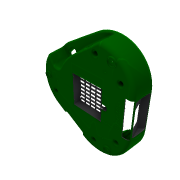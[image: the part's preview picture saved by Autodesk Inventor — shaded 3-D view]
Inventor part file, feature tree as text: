
AUTODESK INVENTOR PART (.ipt)
format: ipt  version: 2016 (Build 200138000, 138)  size: 4,945,408 bytes
history: native  units: in
note: dims shown in document units (in); Inventor stores cm internally (conversion verified against a paired STEP export)
features: projected_geometry x30, sketch x22, extrude x22, fillet x8, other x3, plane x2, thicken_offset x2, reference x2, surface_op x2, chamfer x1, pattern_linear x1, boolean_combine x1, imported_body x1
ambient origin geometry x8: Origin, YZ Plane, XZ Plane, XY Plane, X Axis, Y Axis, Z Axis, Center Point
bodies: Solid1 (feature_tree), Solid2 (feature_tree), Solid3 (feature_tree), Solid4 (feature_tree)
feature tree (97):
  other  "bottom_cover-2016-04-29-21"
  sketch  "Sketch1"  dims[d0=0.0709in d1=0.0709in d2=0.3543in]
  plane  "Work Plane1"
  extrude  "Extrusion1"  Depth=0.0709in
  fillet  "Fillet1"  Radius=0.3543in
  extrude  "Extrusion2"  Depth=1.9685in
  extrude  "Extrusion3"  Depth=0.3937in
  plane  "Work Plane2"
  extrude  "Extrusion4"  Depth=2.5591in TaperAngle=0.0deg
  extrude  "Extrusion5"  Depth=0.7902in
  chamfer  "Chamfer1"  Distance=11.811in
  extrude  "Extrusion6"  Depth=0.0787in
  extrude  "Extrusion7"  Depth=4.9213in TaperAngle=0.0deg
  extrude  "Extrusion8"  Depth=0.0866in TaperAngle=45.0deg
  extrude  "Extrusion9"  Depth=7.874in TaperAngle=0.0deg
  extrude  "Extrusion10"  Depth=4.7244in
  extrude  "Extrusion11"  Depth=0.9843in TaperAngle=0.0deg
  pattern_linear  "Rectangular Pattern1"  Count1=2 Spacing1=0.0in
  boolean_combine  "Combine1"
  extrude  "Extrusion12"  Depth=3.1496in
  extrude  "Extrusion13"  Depth=0.1181in
  extrude  "Extrusion14"  Depth=1.1811in TaperAngle=0.0deg
  extrude  "Extrusion15"  Depth=0.1181in TaperAngle=0.0deg
  fillet  "Fillet2"  Radius=0.0787in
  extrude  "Extrusion16"  Depth=0.1181in
  fillet  "Fillet3"  Radius=1.1811in
  extrude  "Extrusion17"  Depth=0.0394in TaperAngle=0.0deg
  extrude  "Extrusion18"  Depth=0.1575in
  extrude  "Extrusion19"  Depth=0.1181in
  fillet  "Fillet5"  Radius=2.7165in
  fillet  "Fillet6"  Radius=0.1181in
  fillet  "Fillet7"  Radius=0.1181in
  extrude  "Extrusion20"  Depth=0.1181in
  fillet  "Fillet8"  Radius=0.1969in
  thicken_offset  "Thicken1"
  thicken_offset  "Thicken2"
  extrude  "Extrusion21"  Depth=0.1181in
  fillet  "Fillet9"  [1 undecoded]
  extrude  "Extrusion22"  Depth=0.1181in
  imported_body  "Base1"
  reference  "Reference1"
  reference  "Reference2"
  sketch  "Sketch5"  dims[d3=0.3543in d4=1.9685in]
  projected_geometry  "Projected Loop1"
  sketch  "Sketch6"  dims[d5=1.5748in d6=0.3937in d7=-0.0069in]
  projected_geometry  "Projected Loop2"
  sketch  "Sketch7"  dims[d8=0.1969in d9=2.5591in d10=0.0in]
  projected_geometry  "Projected Loop3"
  sketch  "Sketch8"  dims[d11=45.0deg d12=0.7902in d13=11.811in d14=0.0in]
  projected_geometry  "Projected Loop4"
  sketch  "Sketch9"  dims[d15=-0.1181in d16=0.0787in]
  projected_geometry  "Projected Loop5"
  sketch  "Sketch10"  dims[d17=0.0787in d18=4.9213in d19=0.0in]
  projected_geometry  "Projected Loop6"
  sketch  "Sketch11"  dims[d20=0.1969in d21=0.0in d22=0.0866in d23=0.0787in d24=45.0deg]
  projected_geometry  "Projected Loop7"
  sketch  "Sketch12"  dims[d25=7.874in d26=0.0in d27=7.874in d28=0.0in]
  projected_geometry  "Projected Loop8"
  sketch  "Sketch13"  dims[d29=0.2362in d30=0.0in d31=4.7244in]
  projected_geometry  "Projected Loop9"
  projected_geometry  "Projected Loop10"
  sketch  "Sketch14"  dims[d32=4.7244in d33=0.9843in d34=0.0in]
  projected_geometry  "Projected Loop11"
  sketch  "Sketch15"  dims[d35=0.1181in]
  projected_geometry  "Projected Loop12"
  sketch  "Sketch16"  dims[d36=0.9843in d37=0.0in d38=0.7874in d39=0.0in]
  projected_geometry  "Projected Loop13"
  projected_geometry  "Projected Loop14"
  projected_geometry  "Projected Loop15"
  projected_geometry  "Projected Loop16"
  sketch  "Sketch17"  dims[d40=1.9685in d42=0.8661in d43=3.1496in d45=0.5512in]
  projected_geometry  "Projected Loop17"
  sketch  "Sketch18"  dims[d46=0.1181in d47=0.0in d48=1.1811in d49=0.0137in]
  projected_geometry  "Projected Loop18"
  projected_geometry  "Projected Loop19"
  sketch  "Sketch19"  dims[d50=0.9843in d51=1.1811in d52=0.0in]
  projected_geometry  "Projected Loop20"
  sketch  "Sketch20"  dims[d53=0.1181in d54=1.1811in d55=0.0in d56=0.0787in]
  projected_geometry  "Projected Loop21"
  sketch  "Sketch21"  dims[d57=1.1811in d58=0.0in d59=0.1181in d61=1.1811in d62=0.0in]
  projected_geometry  "Projected Loop22"
  sketch  "Sketch22"  dims[d63=1.1811in d64=0.0in d65=0.0394in d66=0.0in]
  projected_geometry  "Projected Loop23"
  projected_geometry  "Projected Loop24"
  projected_geometry  "Projected Loop25"
  sketch  "Sketch24"  dims[d67=0.1969in d68=0.1575in]
  projected_geometry  "Projected Loop27"
  other  "Srf1"
  other  "Srf2"
  sketch  "Sketch25"  dims[d69=0.0472in d70=1.5748in d71=2.7165in d72=0.1181in d73=-0.2061in d74=0.1181in]
  projected_geometry  "Projected Loop28"
  sketch  "Sketch26"  dims[d75=0.1969in d76=0.1969in d77=0.1969in d78=0.1969in d79=0.0in d80=0.1969in d81=0.1969in d82=0.1969in d83=0.1969in d84=0.0in d85=0.0394in d86=0.0394in d87=0.0394in d88=0.0394in d89=0.5315in d90=0.2165in d91=0.1181in d92=0.0in d93=0.0197in d94=1.2205in d95=1.2205in d96=0.2362in d97=0.2362in d98=0.1181in d99=0.0in]
  projected_geometry  "Projected Loop29"
  surface_op  "Boundary Patch2"
  projected_geometry  "Project Cut Edges1"
  projected_geometry  "Project Cut Edges2"
  surface_op  "Boundary Patch1"
note: 1 required parameter value undecoded (feature->parameter linkage not recoverable at this tier; creation-order binding heuristic only, values carry confidence <= 0.55)
